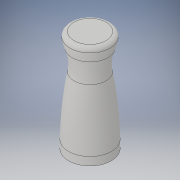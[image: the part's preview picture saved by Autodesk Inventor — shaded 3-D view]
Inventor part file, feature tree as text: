
AUTODESK INVENTOR PART (.ipt)
format: ipt  version: 2019 (Build 230136000, 136)  size: 156,160 bytes
history: native  units: in
note: dims shown in document units (in); Inventor stores cm internally (conversion verified against a paired STEP export)
features: revolve x1, fillet x1, sketch x1
ambient origin geometry x8: Origin, YZ Plane, XZ Plane, XY Plane, X Axis, Y Axis, Z Axis, Center Point
bodies: Solid1 (feature_tree)
feature tree (3):
  revolve  "Revolution1"  [1 undecoded]
  fillet  "Fillet1"  Radius=1.9685in
  sketch  "Sketch1"  dims[d1=0.4134in d2=0.1575in d3=1.9685in d4=0.3937in d5=0.1374in d6=0.3937in d8=0.2693in d9=30.0deg d10=0.7874in d12=0.7874in d13=0.0in d14=90.0deg d15=0.0787in]
note: 1 required parameter value undecoded (feature->parameter linkage not recoverable at this tier; creation-order binding heuristic only, values carry confidence <= 0.55)
